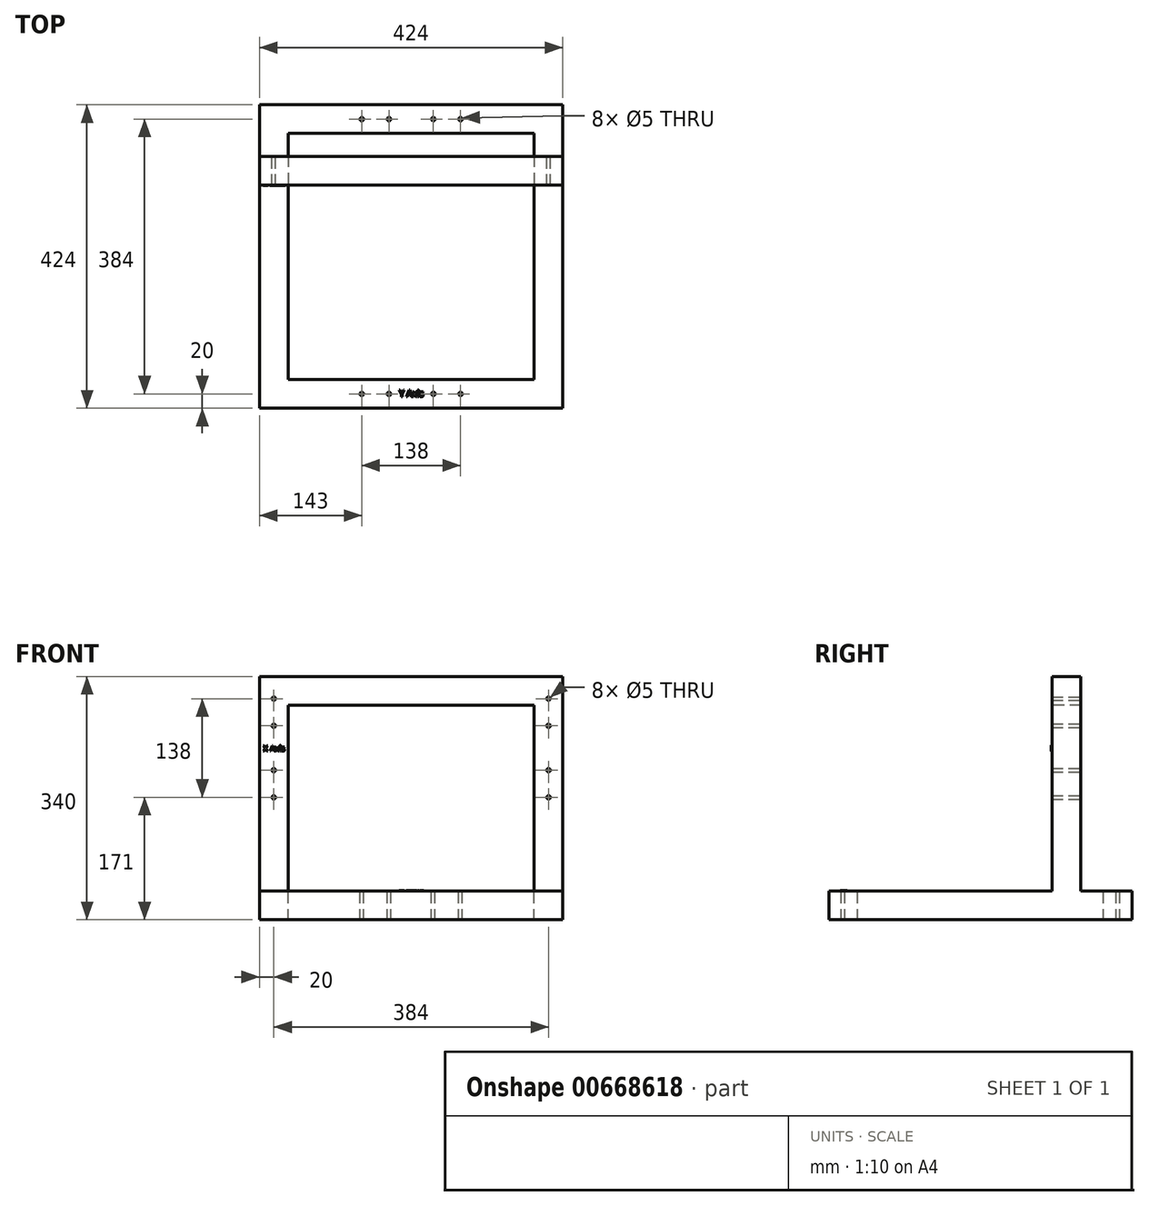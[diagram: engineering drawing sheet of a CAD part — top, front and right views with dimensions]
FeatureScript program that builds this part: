
annotation { "Feature Type Name" : "Feature", "Feature Type Description" : "" }
export const myFeature = defineFeature(function(context is Context, id is Id, definition is map)
    precondition{}
    {
        {
            assignVariable(context, id + "F0", {"name" : "Stand_height", "anyValue" : 300 * mm});
        }
        {
            assignVariable(context, id + "F1", {"name" : "Stand_inner", "anyValue" : 400 - 2 * 8 - 2 * 20});
        }
        {
            var Q0;
            Q0=qCreatedBy(makeId("Top.planeOp"),FACE);
            var sketch = newSketch(context, id + "F2", { "sketchPlane" : qUnion([Q0])});
            skLineSegment(sketch, "E0.bottom", {"start": v(-172, 172) * mm, "end": v(172, 172) * mm});
            skLineSegment(sketch, "E0.top", {"start": v(-172, -172) * mm, "end": v(172, -172) * mm});
            skLineSegment(sketch, "E0.left", {"start": v(-172, 172) * mm, "end": v(-172, -172) * mm});
            skLineSegment(sketch, "E0.right", {"start": v(172, 172) * mm, "end": v(172, -172) * mm});
            skPoint(sketch, "E0.middle", {"position": v(0, 0) * mm});
            skLineSegment(sketch, "E1.bottom", {"start": v(-212, 212) * mm, "end": v(212, 212) * mm});
            skLineSegment(sketch, "E1.top", {"start": v(-212, -212) * mm, "end": v(212, -212) * mm});
            skLineSegment(sketch, "E1.left", {"start": v(-212, 212) * mm, "end": v(-212, -212) * mm});
            skLineSegment(sketch, "E1.right", {"start": v(212, 212) * mm, "end": v(212, -212) * mm});
            skPoint(sketch, "E2", {"position": v(-69, -192) * mm});
            skPoint(sketch, "E3", {"position": v(-31, -192) * mm});
            skPoint(sketch, "E4", {"position": v(-50, -192) * mm});
            skPoint(sketch, "E5.0.1.0", {"position": v(-31, 192) * mm});
            skPoint(sketch, "E5.0.1.1", {"position": v(-50, 192) * mm});
            skPoint(sketch, "E5.0.1.2", {"position": v(-69, 192) * mm});
            skPoint(sketch, "E5.0.1.3", {"position": v(-69, 192) * mm});
            skPoint(sketch, "E5.1.0.0", {"position": v(69, -192) * mm});
            skPoint(sketch, "E5.1.0.1", {"position": v(50, -192) * mm});
            skPoint(sketch, "E5.1.0.2", {"position": v(31, -192) * mm});
            skPoint(sketch, "E5.1.0.3", {"position": v(31, -192) * mm});
            skPoint(sketch, "E5.1.1.0", {"position": v(69, 192) * mm});
            skPoint(sketch, "E5.1.1.1", {"position": v(50, 192) * mm});
            skPoint(sketch, "E5.1.1.2", {"position": v(31, 192) * mm});
            skPoint(sketch, "E5.1.1.3", {"position": v(31, 192) * mm});
            skLineSegment(sketch, "E5.direction1", {"start": v(-69, -192) * mm, "end": v(31, -192) * mm, "construction": true});
            skLineSegment(sketch, "E5.direction2", {"start": v(-69, -192) * mm, "end": v(-69, 192) * mm, "construction": true});
            skSolve(sketch);
        }
        {
            var Q0;
            Q0=makeQuery(id+"F2.imprint","IMPRINT",FACE,{"disambiguationData":[TD([[makeQuery(id+"F2.imprint","IMPRINT",EDGE,{"derivedFrom":sQuery(id+"F2.wireOp",EDGE,"E0.bottom")}),1.0]])]});
            extrude(context, id + "F3", {"entities" : qUnion([Q0]), "oppositeDirection" : true, "depth" : 40 * mm});
        }
        {
            var Q0;
            Q0=qCreatedBy(makeId("Right.planeOp"),FACE);
            var sketch = newSketch(context, id + "F4", { "sketchPlane" : qUnion([Q0])});
            skLineSegment(sketch, "E6.bottom", {"start": v(100, 0) * mm, "end": v(140, 0) * mm});
            skLineSegment(sketch, "E6.top", {"start": v(100, 300) * mm, "end": v(140, 300) * mm});
            skLineSegment(sketch, "E6.left", {"start": v(100, 0) * mm, "end": v(100, 300) * mm});
            skLineSegment(sketch, "E6.right", {"start": v(140, 0) * mm, "end": v(140, 300) * mm});
            skSolve(sketch);
        }
        {
            var Q0;
            Q0=qSketchRegion(id+"F4",true);
            extrude(context, id + "F5", {"entities" : qUnion([Q0]), "depth" : 40 * mm});
        }
        {
            var Q0;
            Q0=makeQuery(id+"F5.opExtrude","SWEPT_BODY",BODY,{"disambiguationData":[OSD([sQuery(id+"F4.wireOp",EDGE,"E6.bottom"),sQuery(id+"F4.wireOp",EDGE,"E6.top"),sQuery(id+"F4.wireOp",EDGE,"E6.left"),sQuery(id+"F4.wireOp",EDGE,"E6.right")])]});
            var Q1;
            Q1=qCreatedBy(makeId("Right.planeOp"),FACE);
            transform(context, id + "F6", {"entities" : qUnion([Q0]), "transformType" : TransformType.TRANSLATION_DISTANCE, "transformDirection" : qUnion([Q1]), "distance" : (getVariable(context, 'Stand_inner') / 2) * mm, "makeCopy" : false});
        }
        {
            var Q0;
            Q0=makeQuery(id+"F5.opExtrude","SWEPT_BODY",BODY,{"disambiguationData":[OSD([sQuery(id+"F4.wireOp",EDGE,"E6.bottom"),sQuery(id+"F4.wireOp",EDGE,"E6.top"),sQuery(id+"F4.wireOp",EDGE,"E6.left"),sQuery(id+"F4.wireOp",EDGE,"E6.right")])]});
            var Q1;
            Q1=qCreatedBy(makeId("Right.planeOp"),FACE);
            mirror(context, id + "F7", {"operationType" : NewBodyOperationType.ADD, "entities" : qUnion([Q0]), "mirrorPlane" : qUnion([Q1])});
        }
        {
            var Q0;
            Q0=qCreatedBy(makeId("Top.planeOp"),FACE);
            cPlane(context, id + "F8", {"entities" : qUnion([Q0]), "cplaneType" : CPlaneType.OFFSET, "offset" : getVariable(context, 'Stand_height'), "width" : 152.4 * mm, "height" : 152.4 * mm});
        }
        {
            var Q0;
            Q0=qCreatedBy(id+"F8.planeOp",FACE);
            var sketch = newSketch(context, id + "F9", { "sketchPlane" : qUnion([Q0])});
            skLineSegment(sketch, "E7.bottom", {"start": v(-172, 140) * mm, "end": v(172, 140) * mm});
            skLineSegment(sketch, "E7.top", {"start": v(-172, 100) * mm, "end": v(172, 100) * mm});
            skLineSegment(sketch, "E7.left", {"start": v(-172, 140) * mm, "end": v(-172, 100) * mm});
            skLineSegment(sketch, "E7.right", {"start": v(172, 140) * mm, "end": v(172, 100) * mm});
            skSolve(sketch);
        }
        {
            var Q0;
            Q0=makeQuery(id+"F9.imprint","IMPRINT",FACE,{"disambiguationData":[TD([[makeQuery(id+"F9.imprint","IMPRINT",EDGE,{"derivedFrom":sQuery(id+"F9.wireOp",EDGE,"E7.bottom")}),-1.0]])]});
            extrude(context, id + "F10", {"entities" : qUnion([Q0]), "operationType" : NewBodyOperationType.ADD, "oppositeDirection" : true, "depth" : 40 * mm});
        }
        {
            var Q0;
            {var subQ0=makeQuery(id+"F5.opExtrude","SWEPT_FACE",FACE,{"disambiguationData":[OSD([sQuery(id+"F4.wireOp",EDGE,"E6.right")])]});Q0=makeQuery(id+"F10.boolean.opBoolean","MERGE",FACE,{"derivedFrom":[subQ0,makeQuery(id+"F7.opPattern","COPY",FACE,{"derivedFrom":subQ0,"instanceName":"1"}),makeQuery(id+"F10.opExtrude","SWEPT_FACE",FACE,{"disambiguationData":[OSD([sQuery(id+"F9.wireOp",EDGE,"E7.bottom")])]})]});}
            var sketch = newSketch(context, id + "F11", { "sketchPlane" : qUnion([Q0])});
            skPoint(sketch, "E8", {"position": v(-192, 269) * mm});
            skPoint(sketch, "E9", {"position": v(-192, 250) * mm});
            skPoint(sketch, "E10", {"position": v(-192, 231) * mm});
            skPoint(sketch, "E11.0.1.0", {"position": v(-192, 131) * mm});
            skPoint(sketch, "E11.0.1.1", {"position": v(-192, 150) * mm});
            skPoint(sketch, "E11.0.1.2", {"position": v(-192, 169) * mm});
            skPoint(sketch, "E11.1.0.0", {"position": v(192, 231) * mm});
            skPoint(sketch, "E11.1.0.1", {"position": v(192, 250) * mm});
            skPoint(sketch, "E11.1.0.2", {"position": v(192, 269) * mm});
            skPoint(sketch, "E11.1.1.0", {"position": v(192, 131) * mm});
            skPoint(sketch, "E11.1.1.1", {"position": v(192, 150) * mm});
            skPoint(sketch, "E11.1.1.2", {"position": v(192, 169) * mm});
            skLineSegment(sketch, "E11.direction1", {"start": v(-192, 231) * mm, "end": v(192, 231) * mm, "construction": true});
            skLineSegment(sketch, "E11.direction2", {"start": v(-192, 231) * mm, "end": v(-192, 131) * mm, "construction": true});
            skSolve(sketch);
        }
        {
            var Q0;
            Q0=sQuery(id+"F2.wireOp",VERTEX,"E2");
            var Q1;
            Q1=sQuery(id+"F2.wireOp",VERTEX,"E3");
            var Q2;
            Q2=sQuery(id+"F2.wireOp",VERTEX,"E5.1.0.2");
            var Q3;
            Q3=sQuery(id+"F2.wireOp",VERTEX,"E5.1.0.0");
            var Q4;
            Q4=sQuery(id+"F2.wireOp",VERTEX,"E5.0.1.2");
            var Q5;
            Q5=sQuery(id+"F2.wireOp",VERTEX,"E5.0.1.0");
            var Q6;
            Q6=sQuery(id+"F2.wireOp",VERTEX,"E5.1.1.2");
            var Q7;
            Q7=sQuery(id+"F2.wireOp",VERTEX,"E5.1.1.0");
            var Q8;
            Q8=sQuery(id+"F11.wireOp",VERTEX,"E8");
            var Q9;
            Q9=sQuery(id+"F11.wireOp",VERTEX,"E10");
            var Q10;
            Q10=sQuery(id+"F11.wireOp",VERTEX,"E11.0.1.2");
            var Q11;
            Q11=sQuery(id+"F11.wireOp",VERTEX,"E11.0.1.0");
            var Q12;
            Q12=sQuery(id+"F11.wireOp",VERTEX,"E11.1.0.2");
            var Q13;
            Q13=sQuery(id+"F11.wireOp",VERTEX,"E11.1.0.0");
            var Q14;
            Q14=sQuery(id+"F11.wireOp",VERTEX,"E11.1.1.2");
            var Q15;
            Q15=sQuery(id+"F11.wireOp",VERTEX,"E11.1.1.0");
            var Q16;
            Q16=makeQuery(id+"F3.opExtrude","SWEPT_BODY",BODY,{"disambiguationData":[OSD([sQuery(id+"F2.wireOp",EDGE,"E0.bottom"),sQuery(id+"F2.wireOp",EDGE,"E0.top"),sQuery(id+"F2.wireOp",EDGE,"E0.left"),sQuery(id+"F2.wireOp",EDGE,"E0.right"),sQuery(id+"F2.wireOp",EDGE,"E1.bottom"),sQuery(id+"F2.wireOp",EDGE,"E1.top"),sQuery(id+"F2.wireOp",EDGE,"E1.left"),sQuery(id+"F2.wireOp",EDGE,"E1.right")])]});
            hole(context, id + "F12", {"style" : HoleStyle.SIMPLE, "endStyle" : HoleEndStyle.THROUGH, "holeDiameter" : 5 * mm, "isTappedThrough" : true, "tappedDepth" : 12 * mm, "tapClearance" : 3, "locations" : qUnion([Q0, Q1, Q2, Q3, Q4, Q5, Q6, Q7, Q8, Q9, Q10, Q11, Q12, Q13, Q14, Q15]), "scope" : qUnion([Q16])});
        }
        {
            var Q0;
            {var subQ0=makeQuery(id+"F5.opExtrude","SWEPT_FACE",FACE,{"disambiguationData":[OSD([sQuery(id+"F4.wireOp",EDGE,"E6.left")])]});Q0=makeQuery(id+"F10.boolean.opBoolean","MERGE",FACE,{"derivedFrom":[subQ0,makeQuery(id+"F7.opPattern","COPY",FACE,{"derivedFrom":subQ0,"instanceName":"1"}),makeQuery(id+"F10.opExtrude","SWEPT_FACE",FACE,{"disambiguationData":[OSD([sQuery(id+"F9.wireOp",EDGE,"E7.top")])]})]});}
            var sketch = newSketch(context, id + "F13", { "sketchPlane" : qUnion([Q0])});
            skText(sketch, "E12", { "text": "X Axis\n", "fontName": "OpenSans-Regular.ttf"});
            const initialGuessF13  = {"E12": [-0.20674, 0.19548, 1, 0, 0.00804]};
            skSetInitialGuess(sketch, initialGuessF13);
            skSolve(sketch);
        }
        {
            var Q0;
            {var subQ5=sQuery(id+"F2.wireOp",EDGE,"E0.right");var subQ6=sQuery(id+"F2.wireOp",EDGE,"E1.right");var subQ7=sQuery(id+"F2.wireOp",EDGE,"E1.left");var subQ10=sQuery(id+"F2.wireOp",EDGE,"E0.top");var subQ11=sQuery(id+"F2.wireOp",EDGE,"E0.left");var subQ12=sQuery(id+"F2.wireOp",EDGE,"E1.top");Q0=makeQuery(id+"F7.boolean.opBoolean","SPLIT",FACE,{"disambiguationData":[TD([makeQuery(id+"F3.opExtrude","SWEPT_FACE",FACE,{"disambiguationData":[OSD([subQ10])]})])],"derivedFrom":makeQuery(id+"F3.opExtrude","CAP_FACE",FACE,{"disambiguationData":[OSD([sQuery(id+"F2.wireOp",EDGE,"E0.bottom"),subQ10,subQ11,subQ5,sQuery(id+"F2.wireOp",EDGE,"E1.bottom"),subQ12,subQ7,subQ6])],"isStart":true})});}
            var sketch = newSketch(context, id + "F14", { "sketchPlane" : qUnion([Q0])});
            skText(sketch, "E13", { "text": "Y Axis", "fontName": "OpenSans-Regular.ttf"});
            const initialGuessF14  = {"E13": [-0.01672, -0.19582, 1, 0, 0.0091]};
            skSetInitialGuess(sketch, initialGuessF14);
            skSolve(sketch);
        }
        {
            var Q0;
            Q0=qSketchRegion(id+"F14",true);
            extrude(context, id + "F15", {"entities" : qUnion([Q0]), "operationType" : NewBodyOperationType.ADD, "depth" : 1 * mm});
        }
        {
            var Q0;
            Q0=qSketchRegion(id+"F13",true);
            extrude(context, id + "F16", {"entities" : qUnion([Q0]), "operationType" : NewBodyOperationType.ADD, "depth" : 1 * mm});
        }
    });
